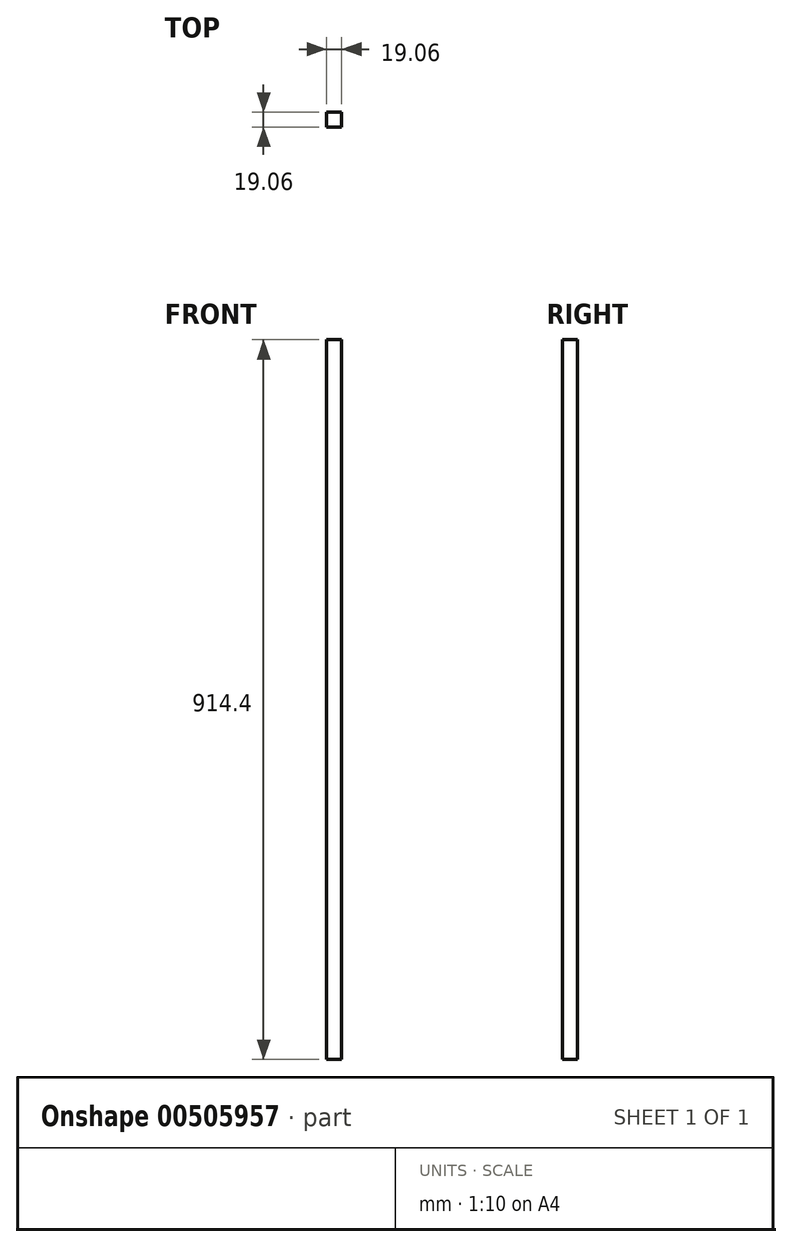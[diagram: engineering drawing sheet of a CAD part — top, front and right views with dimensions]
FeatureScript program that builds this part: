
annotation { "Feature Type Name" : "Feature", "Feature Type Description" : "" }
export const myFeature = defineFeature(function(context is Context, id is Id, definition is map)
    precondition{}
    {
        {
            var Q0;
            Q0=qCreatedBy(makeId("Top.planeOp"),FACE);
            var sketch = newSketch(context, id + "F0", { "sketchPlane" : qUnion([Q0])});
            skLineSegment(sketch, "E0.bottom", {"start": v(-9.52, 9.52) * mm, "end": v(9.53, 9.52) * mm});
            skLineSegment(sketch, "E0.top", {"start": v(-9.53, -9.53) * mm, "end": v(9.52, -9.53) * mm});
            skLineSegment(sketch, "E0.left", {"start": v(-9.52, 9.52) * mm, "end": v(-9.53, -9.53) * mm});
            skLineSegment(sketch, "E0.right", {"start": v(9.53, 9.52) * mm, "end": v(9.52, -9.53) * mm});
            skPoint(sketch, "E0.middle", {"position": v(0, 0) * mm});
            skSolve(sketch);
        }
        {
            var Q0;
            Q0=qSketchRegion(id+"F0",true);
            extrude(context, id + "F1", {"entities" : qUnion([Q0]), "depth" : 914.4 * mm});
        }
    });
